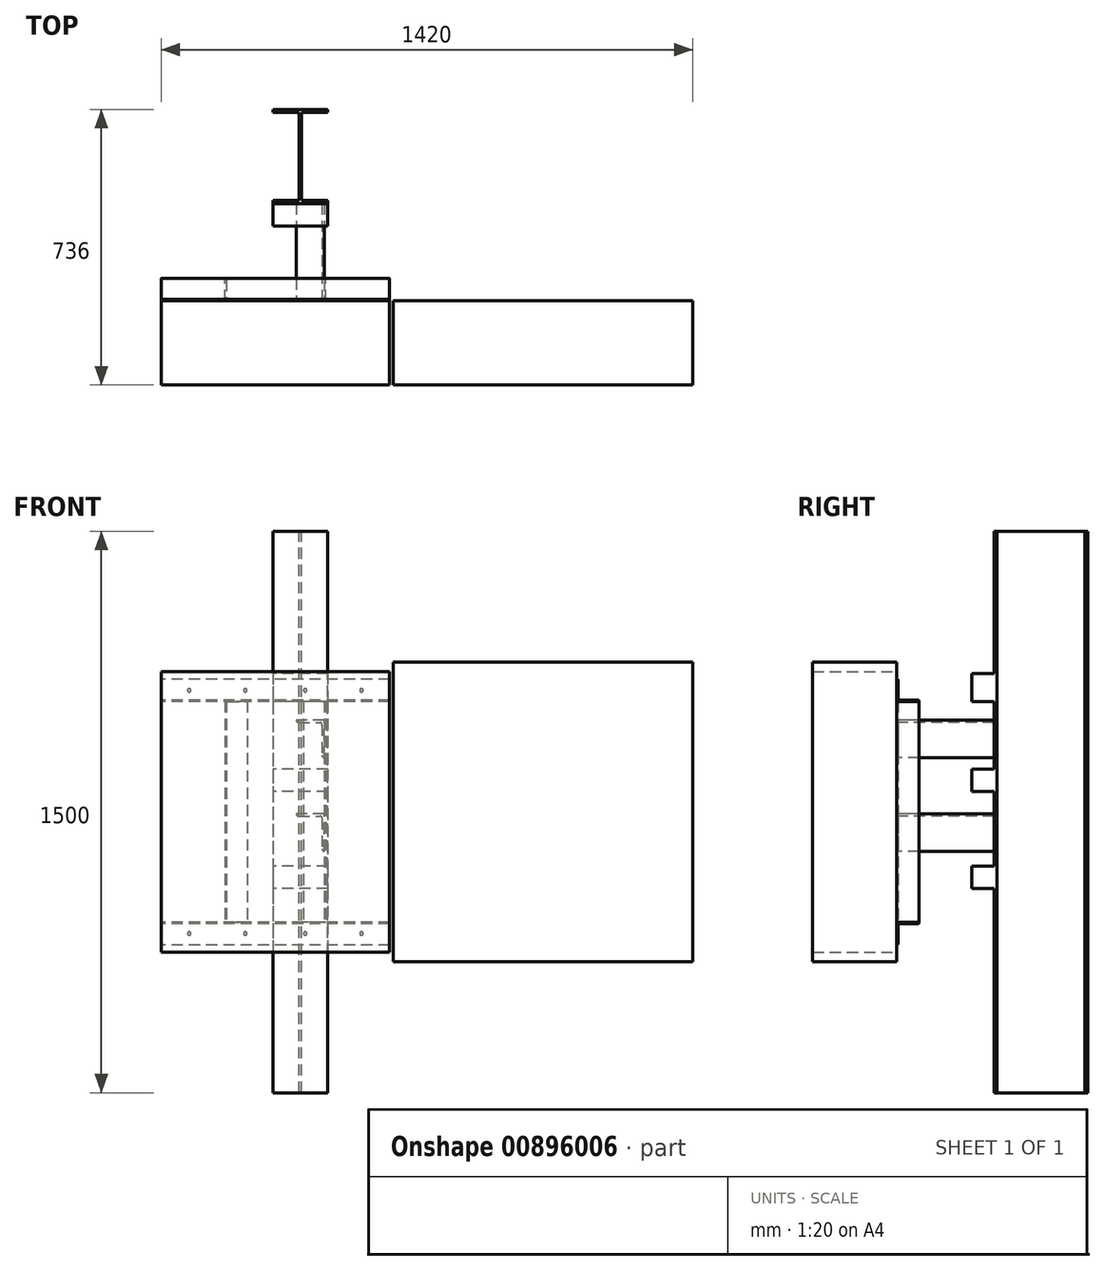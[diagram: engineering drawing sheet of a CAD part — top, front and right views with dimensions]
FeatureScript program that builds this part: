
annotation { "Feature Type Name" : "Feature", "Feature Type Description" : "" }
export const myFeature = defineFeature(function(context is Context, id is Id, definition is map)
    precondition{}
    {
        {
            var Q0;
            Q0=qCreatedBy(makeId("Right.planeOp"),FACE);
            var sketch = newSketch(context, id + "F0", { "sketchPlane" : qUnion([Q0])});
            skLineSegment(sketch, "E0", {"start": v(0, -295) * mm, "end": v(60, -295) * mm});
            skLineSegment(sketch, "E1", {"start": v(56, -299) * mm, "end": v(8, -299) * mm});
            skLineSegment(sketch, "E2", {"start": v(4, -303) * mm, "end": v(4, -351) * mm});
            skLineSegment(sketch, "E3", {"start": v(0, -355) * mm, "end": v(0, -355) * mm});
            skLineSegment(sketch, "E4", {"start": v(0, -355) * mm, "end": v(0, -295) * mm});
            skArc(sketch, "E5.filletArc", {"start": v(56, -299) * mm, "mid": v(58.83, -297.83) * mm, "end": v(60, -295) * mm});
            skArc(sketch, "E6.filletArc", {"start": v(8, -299) * mm, "mid": v(5.17, -300.17) * mm, "end": v(4, -303) * mm});
            skArc(sketch, "E7.filletArc", {"start": v(0, -355) * mm, "mid": v(2.83, -353.83) * mm, "end": v(4, -351) * mm});
            skPoint(sketch, "E8", {"position": v(0, -325) * mm});
            skArc(sketch, "E9.MirrorCS", {"start": v(56, 299) * mm, "mid": v(58.83, 297.83) * mm, "end": v(60, 295) * mm});
            skArc(sketch, "E10.MirrorCS", {"start": v(8, 299) * mm, "mid": v(5.17, 300.17) * mm, "end": v(4, 303) * mm});
            skArc(sketch, "E11.MirrorCS", {"start": v(0, 355) * mm, "mid": v(2.83, 353.83) * mm, "end": v(4, 351) * mm});
            skLineSegment(sketch, "E12.MirrorCS", {"start": v(4, 303) * mm, "end": v(4, 351) * mm});
            skLineSegment(sketch, "E13.MirrorCS", {"start": v(0, 355) * mm, "end": v(0, 295) * mm});
            skLineSegment(sketch, "E14.MirrorCS", {"start": v(0, 355) * mm, "end": v(0, 355) * mm});
            skLineSegment(sketch, "E15.MirrorCS", {"start": v(56, 299) * mm, "end": v(8, 299) * mm});
            skLineSegment(sketch, "E16.MirrorCS", {"start": v(0, 295) * mm, "end": v(60, 295) * mm});
            skPoint(sketch, "E17.MirrorP", {"position": v(0, 325) * mm});
            skSolve(sketch);
        }
        {
            var Q0;
            Q0 = qSketchRegion(id + "F0", true);
            extrude(context, id + "F1", {"entities" : qUnion([Q0]), "endBound" : BoundingType.SYMMETRIC, "depth" : 610 * mm, "offsetDistance" : 25 * mm});
        }
        {
            var Q0;
            Q0=makeQuery(id+"F1.opExtrude","SWEPT_FACE",FACE,{"disambiguationData":[OSD([sQuery(id+"F0.wireOp",EDGE,"E0")])]});
            var sketch = newSketch(context, id + "F2", { "sketchPlane" : qUnion([Q0])});
            skArc(sketch, "E18.MirrorCS", {"start": v(131, 56) * mm, "mid": v(132.17, 58.83) * mm, "end": v(135, 60) * mm});
            skArc(sketch, "E19.MirrorCS", {"start": v(131, 8) * mm, "mid": v(129.83, 5.17) * mm, "end": v(127, 4) * mm});
            skArc(sketch, "E20.MirrorCS", {"start": v(75, 0) * mm, "mid": v(76.17, 2.83) * mm, "end": v(79, 4) * mm});
            skLineSegment(sketch, "E21.MirrorCS", {"start": v(127, 4) * mm, "end": v(79, 4) * mm});
            skLineSegment(sketch, "E22.MirrorCS", {"start": v(75, 0) * mm, "end": v(135, 0) * mm});
            skLineSegment(sketch, "E23.MirrorCS", {"start": v(131, 56) * mm, "end": v(131, 8) * mm});
            skLineSegment(sketch, "E24.MirrorCS", {"start": v(135, 0) * mm, "end": v(135, 60) * mm});
            skPoint(sketch, "E25.MirrorP", {"position": v(105, 0) * mm});
            skArc(sketch, "E26.MirrorCS", {"start": v(-75, 0) * mm, "mid": v(-76.17, 2.83) * mm, "end": v(-79, 4) * mm});
            skArc(sketch, "E27.MirrorCS", {"start": v(-131, 8) * mm, "mid": v(-129.83, 5.17) * mm, "end": v(-127, 4) * mm});
            skArc(sketch, "E28.MirrorCS", {"start": v(-131, 56) * mm, "mid": v(-132.17, 58.83) * mm, "end": v(-135, 60) * mm});
            skLineSegment(sketch, "E29.MirrorCS", {"start": v(-135, 0) * mm, "end": v(-135, 60) * mm});
            skPoint(sketch, "E30.MirrorP", {"position": v(-105, 0) * mm});
            skLineSegment(sketch, "E31.MirrorCS", {"start": v(-127, 4) * mm, "end": v(-79, 4) * mm});
            skLineSegment(sketch, "E32.MirrorCS", {"start": v(-75, 0) * mm, "end": v(-135, 0) * mm});
            skLineSegment(sketch, "E33.MirrorCS", {"start": v(-131, 56) * mm, "end": v(-131, 8) * mm});
            skSolve(sketch);
        }
        {
            var Q0;
            Q0 = qSketchRegion(id + "F2", true);
            var Q1;
            Q1=makeQuery(id+"F1.opExtrude","SWEPT_FACE",FACE,{"disambiguationData":[OSD([sQuery(id+"F0.wireOp",EDGE,"E16.MirrorCS")])]});
            extrude(context, id + "F3", {"entities" : qUnion([Q0]), "endBound" : BoundingType.UP_TO_SURFACE, "depth" : 25 * mm, "endBoundEntityFace" : qUnion([Q1]), "offsetDistance" : 25 * mm});
        }
        {
            var Q0;
            Q0=makeQuery(id+"F1.opExtrude","SWEPT_FACE",FACE,{"disambiguationData":[OSD([sQuery(id+"F0.wireOp",EDGE,"E13.MirrorCS")])]});
            var sketch = newSketch(context, id + "F4", { "sketchPlane" : qUnion([Q0])});
            skLineSegment(sketch, "E34", {"start": v(305, 325) * mm, "end": v(-305, 325) * mm, "construction": true});
            skLineSegment(sketch, "E35", {"start": v(-305, -325) * mm, "end": v(305, -325) * mm, "construction": true});
            skPoint(sketch, "E36", {"position": v(230, 325) * mm});
            skPoint(sketch, "E37", {"position": v(80, 325) * mm});
            skPoint(sketch, "E38", {"position": v(-80, 325) * mm});
            skPoint(sketch, "E39", {"position": v(-230, 325) * mm});
            skPoint(sketch, "E40", {"position": v(-230, -325) * mm});
            skPoint(sketch, "E41", {"position": v(-80, -325) * mm});
            skPoint(sketch, "E42", {"position": v(80, -325) * mm});
            skPoint(sketch, "E43", {"position": v(230, -325) * mm});
            skSolve(sketch);
        }
        {
            var Q0;
            Q0=sQuery(id+"F4.wireOp",VERTEX,"E39");
            var Q1;
            Q1=sQuery(id+"F4.wireOp",VERTEX,"E38");
            var Q2;
            Q2=sQuery(id+"F4.wireOp",VERTEX,"E37");
            var Q3;
            Q3=sQuery(id+"F4.wireOp",VERTEX,"E36");
            var Q4;
            Q4=sQuery(id+"F4.wireOp",VERTEX,"E41");
            var Q5;
            Q5=sQuery(id+"F4.wireOp",VERTEX,"E42");
            var Q6;
            Q6=sQuery(id+"F4.wireOp",VERTEX,"E40");
            var Q7;
            Q7=sQuery(id+"F4.wireOp",VERTEX,"E43");
            var Q8;
            Q8=makeQuery(id+"F1.opExtrude","SWEPT_BODY",BODY,{"disambiguationData":[OSD([sQuery(id+"F0.wireOp",EDGE,"E9.MirrorCS"),sQuery(id+"F0.wireOp",EDGE,"E10.MirrorCS"),sQuery(id+"F0.wireOp",EDGE,"E11.MirrorCS"),sQuery(id+"F0.wireOp",EDGE,"E12.MirrorCS"),sQuery(id+"F0.wireOp",EDGE,"E13.MirrorCS"),sQuery(id+"F0.wireOp",EDGE,"E15.MirrorCS"),sQuery(id+"F0.wireOp",EDGE,"E16.MirrorCS")])]});
            var Q9;
            Q9=makeQuery(id+"F1.opExtrude","SWEPT_BODY",BODY,{"disambiguationData":[OSD([sQuery(id+"F0.wireOp",EDGE,"E0"),sQuery(id+"F0.wireOp",EDGE,"E1"),sQuery(id+"F0.wireOp",EDGE,"E2"),sQuery(id+"F0.wireOp",EDGE,"E4"),sQuery(id+"F0.wireOp",EDGE,"E5.filletArc"),sQuery(id+"F0.wireOp",EDGE,"E6.filletArc"),sQuery(id+"F0.wireOp",EDGE,"E7.filletArc")])]});
            hole(context, id + "F5", {"style" : HoleStyle.SIMPLE, "endStyle" : HoleEndStyle.THROUGH, "standardTappedOrClearance" : lookupTablePath({ "fit" : "Normal", "standard" : "ISO", "size" : "M8", "type" : "Clearance" }), "standardBlindInLast" : lookupTablePath({ "fit" : "Normal", "standard" : "ISO", "size" : "M8", "type" : "Clearance" }), "holeDiameter" : 9 * mm, "majorDiameter" : 5 * mm, "isTappedThrough" : true, "tappedDepth" : 12 * mm, "tapClearance" : 3, "startFromSketch" : true, "locations" : qUnion([Q0, Q1, Q2, Q3, Q4, Q5, Q6, Q7]), "scope" : qUnion([Q8, Q9])});
        }
        {
            var Q0;
            Q0=makeQuery(id+"F1.opExtrude","SWEPT_FACE",FACE,{"disambiguationData":[OSD([sQuery(id+"F0.wireOp",EDGE,"E13.MirrorCS")])]});
            var sketch = newSketch(context, id + "F6", { "sketchPlane" : qUnion([Q0])});
            skLineSegment(sketch, "E44.bottom", {"start": v(-305, 375) * mm, "end": v(305, 375) * mm});
            skLineSegment(sketch, "E44.top", {"start": v(-305, -375) * mm, "end": v(305, -375) * mm});
            skLineSegment(sketch, "E44.left", {"start": v(-305, 375) * mm, "end": v(-305, -375) * mm});
            skLineSegment(sketch, "E44.right", {"start": v(305, 375) * mm, "end": v(305, -375) * mm});
            skPoint(sketch, "E44.middle", {"position": v(0, 0) * mm});
            skSolve(sketch);
        }
        {
            var Q0;
            Q0 = qSketchRegion(id + "F6", true);
            extrude(context, id + "F7", {"entities" : qUnion([Q0]), "depth" : 200 * mm, "offsetDistance" : 25 * mm});
        }
        {
            var Q0;
            Q0=makeQuery(id+"F7.opExtrude","CAP_FACE",FACE,{"disambiguationData":[OSD([sQuery(id+"F6.wireOp",EDGE,"E44.bottom"),sQuery(id+"F6.wireOp",EDGE,"E44.top"),sQuery(id+"F6.wireOp",EDGE,"E44.left"),sQuery(id+"F6.wireOp",EDGE,"E44.right")])],"isStart":false});
            extrude(context, id + "F8", {"entities" : qUnion([Q0]), "operationType" : NewBodyOperationType.ADD, "depth" : 25 * mm, "offsetDistance" : 25 * mm});
        }
        {
            var Q0;
            Q0=makeQuery(id+"F8.opExtrude","CAP_FACE",FACE,{"disambiguationData":[OSD([sQuery(id+"F6.wireOp",EDGE,"E44.bottom"),sQuery(id+"F6.wireOp",EDGE,"E44.top"),sQuery(id+"F6.wireOp",EDGE,"E44.left"),sQuery(id+"F6.wireOp",EDGE,"E44.right")])],"isStart":false});
            var sketch = newSketch(context, id + "F9", { "sketchPlane" : qUnion([Q0])});
            skLineSegment(sketch, "E45.bottom", {"start": v(315, 400) * mm, "end": v(1115, 400) * mm});
            skLineSegment(sketch, "E45.top", {"start": v(315, -400) * mm, "end": v(1115, -400) * mm});
            skLineSegment(sketch, "E45.left", {"start": v(315, 400) * mm, "end": v(315, -400) * mm});
            skLineSegment(sketch, "E45.right", {"start": v(1115, 400) * mm, "end": v(1115, -400) * mm});
            skPoint(sketch, "E45.middle", {"position": v(715, 0) * mm});
            skSolve(sketch);
        }
        {
            var Q0;
            Q0 = qSketchRegion(id + "F9", true);
            var Q1;
            Q1=makeQuery(id+"F7.opExtrude","CAP_FACE",FACE,{"disambiguationData":[OSD([sQuery(id+"F6.wireOp",EDGE,"E44.bottom"),sQuery(id+"F6.wireOp",EDGE,"E44.top"),sQuery(id+"F6.wireOp",EDGE,"E44.left"),sQuery(id+"F6.wireOp",EDGE,"E44.right")])],"isStart":true});
            extrude(context, id + "F10", {"entities" : qUnion([Q0]), "endBound" : BoundingType.UP_TO_SURFACE, "oppositeDirection" : true, "depth" : 25 * mm, "endBoundEntityFace" : qUnion([Q1]), "offsetDistance" : 25 * mm});
        }
        {
            var Q0;
            Q0=qCreatedBy(makeId("Top.planeOp"),FACE);
            var sketch = newSketch(context, id + "F11", { "sketchPlane" : qUnion([Q0])});
            skLineSegment(sketch, "E46.bottom", {"start": v(-6, 260) * mm, "end": v(140, 260) * mm});
            skLineSegment(sketch, "E46.top", {"start": v(-6, 511) * mm, "end": v(140, 511) * mm});
            skLineSegment(sketch, "E46.left", {"start": v(-6, 260) * mm, "end": v(-6, 511) * mm});
            skLineSegment(sketch, "E46.right", {"start": v(140, 260) * mm, "end": v(140, 511) * mm});
            skPoint(sketch, "E46.middle", {"position": v(67, 385.5) * mm});
            skSolve(sketch);
        }
        {
            var Q0;
            Q0 = qSketchRegion(id + "F11", true);
            extrude(context, id + "F12", {"entities" : qUnion([Q0]), "endBound" : BoundingType.SYMMETRIC, "depth" : 1500 * mm, "offsetDistance" : 25 * mm});
        }
        {
            var Q0;
            Q0=makeQuery(id+"F12.opExtrude","CAP_FACE",FACE,{"disambiguationData":[OSD([sQuery(id+"F11.wireOp",EDGE,"E46.bottom"),sQuery(id+"F11.wireOp",EDGE,"E46.top"),sQuery(id+"F11.wireOp",EDGE,"E46.left"),sQuery(id+"F11.wireOp",EDGE,"E46.right")])],"isStart":false});
            var sketch = newSketch(context, id + "F13", { "sketchPlane" : qUnion([Q0])});
            skLineSegment(sketch, "E47.bottom", {"start": v(70.15, 268) * mm, "end": v(209.85, 268) * mm});
            skLineSegment(sketch, "E47.top", {"start": v(70.15, 503) * mm, "end": v(209.85, 503) * mm});
            skLineSegment(sketch, "E47.left", {"start": v(70.15, 268) * mm, "end": v(70.15, 503) * mm});
            skLineSegment(sketch, "E47.right", {"start": v(209.85, 268) * mm, "end": v(209.85, 503) * mm});
            skPoint(sketch, "E47.middle", {"position": v(140, 385.5) * mm});
            skLineSegment(sketch, "E48.bottom", {"start": v(63.85, 268) * mm, "end": v(-75.85, 268) * mm});
            skLineSegment(sketch, "E48.top", {"start": v(63.85, 503) * mm, "end": v(-75.85, 503) * mm});
            skLineSegment(sketch, "E48.left", {"start": v(63.85, 268) * mm, "end": v(63.85, 503) * mm});
            skLineSegment(sketch, "E48.right", {"start": v(-75.85, 268) * mm, "end": v(-75.85, 503) * mm});
            skPoint(sketch, "E48.middle", {"position": v(-6, 385.5) * mm});
            skSolve(sketch);
        }
        {
            var Q0;
            Q0 = qSketchRegion(id + "F13", true);
            extrude(context, id + "F14", {"entities" : qUnion([Q0]), "operationType" : NewBodyOperationType.REMOVE, "endBound" : BoundingType.THROUGH_ALL, "oppositeDirection" : true, "depth" : 25 * mm, "offsetDistance" : 25 * mm});
        }
        {
            var Q0;
            Q0=makeQuery(id+"F12.opExtrude","SWEPT_FACE",FACE,{"disambiguationData":[OSD([sQuery(id+"F11.wireOp",EDGE,"E46.bottom")])]});
            var sketch = newSketch(context, id + "F15", { "sketchPlane" : qUnion([Q0])});
            skLineSegment(sketch, "E49.bottom", {"start": v(140, 295) * mm, "end": v(-6, 295) * mm});
            skLineSegment(sketch, "E49.top", {"start": v(140, 370) * mm, "end": v(-6, 370) * mm});
            skLineSegment(sketch, "E49.left", {"start": v(140, 295) * mm, "end": v(140, 370) * mm});
            skLineSegment(sketch, "E49.right", {"start": v(-6, 295) * mm, "end": v(-6, 370) * mm});
            skPoint(sketch, "E49.middle", {"position": v(67, 332.5) * mm});
            skLineSegment(sketch, "E50.bottom", {"start": v(140, 55) * mm, "end": v(-6, 55) * mm});
            skLineSegment(sketch, "E50.top", {"start": v(140, 115) * mm, "end": v(-6, 115) * mm});
            skLineSegment(sketch, "E50.left", {"start": v(140, 55) * mm, "end": v(140, 115) * mm});
            skLineSegment(sketch, "E50.right", {"start": v(-6, 55) * mm, "end": v(-6, 115) * mm});
            skPoint(sketch, "E50.middle", {"position": v(67, 85) * mm});
            skLineSegment(sketch, "E51.bottom", {"start": v(140, -205) * mm, "end": v(-6, -205) * mm});
            skLineSegment(sketch, "E51.top", {"start": v(140, -145) * mm, "end": v(-6, -145) * mm});
            skLineSegment(sketch, "E51.left", {"start": v(140, -205) * mm, "end": v(140, -145) * mm});
            skLineSegment(sketch, "E51.right", {"start": v(-6, -205) * mm, "end": v(-6, -145) * mm});
            skPoint(sketch, "E51.middle", {"position": v(67, -175) * mm});
            skSolve(sketch);
        }
        {
            var Q0;
            Q0 = qSketchRegion(id + "F15", true);
            extrude(context, id + "F16", {"entities" : qUnion([Q0]), "operationType" : NewBodyOperationType.ADD, "depth" : 60 * mm, "offsetDistance" : 25 * mm});
        }
        {
            var Q0;
            Q0=makeQuery(id+"F3.opExtrude","SWEPT_FACE",FACE,{"disambiguationData":[OSD([sQuery(id+"F2.wireOp",EDGE,"E21.MirrorCS")])]});
            var sketch = newSketch(context, id + "F17", { "sketchPlane" : qUnion([Q0])});
            skLineSegment(sketch, "E52", {"start": v(-131, 145) * mm, "end": v(-131, 245) * mm});
            skLineSegment(sketch, "E53", {"start": v(-131, 245) * mm, "end": v(-56, 245) * mm});
            skLineSegment(sketch, "E54", {"start": v(-56, 245) * mm, "end": v(-56, 245) * mm});
            skLineSegment(sketch, "E55", {"start": v(-62, 239) * mm, "end": v(-119, 239) * mm});
            skLineSegment(sketch, "E56", {"start": v(-125, 233) * mm, "end": v(-125, 151) * mm});
            skPoint(sketch, "E57.visualSharp", {"position": v(-56, 239) * mm});
            skArc(sketch, "E57.filletArc", {"start": v(-62, 239) * mm, "mid": v(-57.76, 240.76) * mm, "end": v(-56, 245) * mm});
            skArc(sketch, "E58.filletArc", {"start": v(-131, 145) * mm, "mid": v(-126.76, 146.76) * mm, "end": v(-125, 151) * mm});
            skPoint(sketch, "E59.visualSharp", {"position": v(-125, 239) * mm});
            skArc(sketch, "E59.filletArc", {"start": v(-119, 239) * mm, "mid": v(-123.24, 237.24) * mm, "end": v(-125, 233) * mm});
            skPoint(sketch, "E60.0.1.0", {"position": v(-125, -11) * mm});
            skLineSegment(sketch, "E60.0.1.1", {"start": v(-125, -17) * mm, "end": v(-125, -99) * mm});
            skPoint(sketch, "E60.0.1.2", {"position": v(-56, -11) * mm});
            skArc(sketch, "E60.0.1.3", {"start": v(-131, -105) * mm, "mid": v(-126.76, -103.24) * mm, "end": v(-125, -99) * mm});
            skLineSegment(sketch, "E60.0.1.4", {"start": v(-131, -5) * mm, "end": v(-56, -5) * mm});
            skLineSegment(sketch, "E60.0.1.5", {"start": v(-131, -105) * mm, "end": v(-131, -5) * mm});
            skLineSegment(sketch, "E60.0.1.6", {"start": v(-62, -11) * mm, "end": v(-119, -11) * mm});
            skArc(sketch, "E60.0.1.7", {"start": v(-119, -11) * mm, "mid": v(-123.24, -12.76) * mm, "end": v(-125, -17) * mm});
            skArc(sketch, "E60.0.1.8", {"start": v(-62, -11) * mm, "mid": v(-57.76, -9.24) * mm, "end": v(-56, -5) * mm});
            skLineSegment(sketch, "E60.direction1", {"start": v(-131, 145) * mm, "end": v(-106, 145) * mm, "construction": true});
            skLineSegment(sketch, "E60.direction2", {"start": v(-131, 145) * mm, "end": v(-131, -105) * mm, "construction": true});
            skSolve(sketch);
        }
        {
            var Q0;
            Q0 = qSketchRegion(id + "F17", true);
            var Q1;
            {var subQ2=sQuery(id+"F11.wireOp",EDGE,"E46.bottom");Q1=makeQuery(id+"F16.boolean.opBoolean","SPLIT",FACE,{"disambiguationData":[TD([makeQuery(id+"F16.opExtrude","SWEPT_FACE",FACE,{"disambiguationData":[OSD([sQuery(id+"F15.wireOp",EDGE,"E49.top")])]})])],"derivedFrom":makeQuery(id+"F12.opExtrude","SWEPT_FACE",FACE,{"disambiguationData":[OSD([subQ2])]})});}
            extrude(context, id + "F18", {"entities" : qUnion([Q0]), "endBound" : BoundingType.UP_TO_SURFACE, "depth" : 25 * mm, "endBoundEntityFace" : qUnion([Q1]), "offsetDistance" : 25 * mm});
        }
    });
